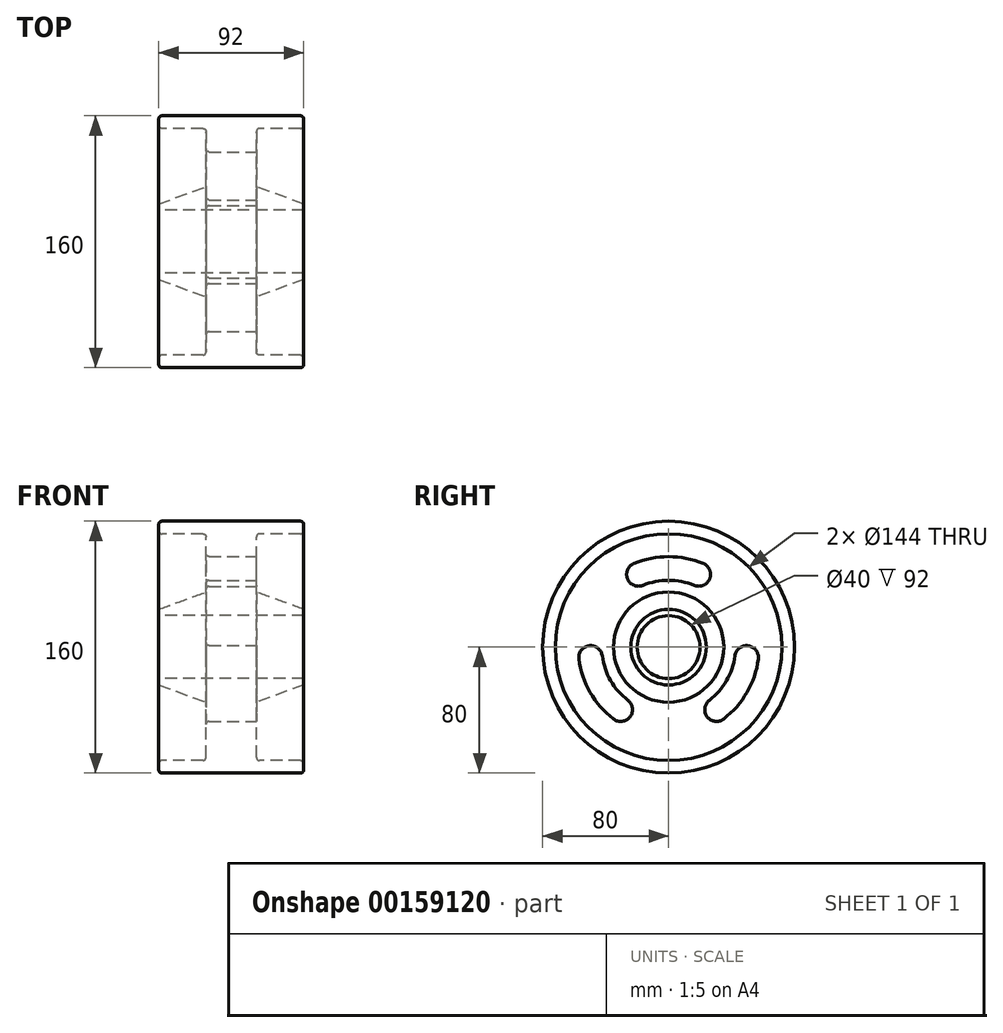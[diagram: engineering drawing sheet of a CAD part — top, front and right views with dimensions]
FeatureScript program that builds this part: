
annotation { "Feature Type Name" : "Feature", "Feature Type Description" : "" }
export const myFeature = defineFeature(function(context is Context, id is Id, definition is map)
    precondition{}
    {
        {
            var Q0;
            Q0=qCreatedBy(makeId("Front.planeOp"),FACE);
            var sketch = newSketch(context, id + "F0", { "sketchPlane" : qUnion([Q0])});
            skLineSegment(sketch, "E0.bottom", {"start": v(0, 0) * mm, "end": v(92, 0) * mm});
            skLineSegment(sketch, "E0.top", {"start": v(0, 80) * mm, "end": v(92, 80) * mm});
            skLineSegment(sketch, "E0.left", {"start": v(0, 0) * mm, "end": v(0, 80) * mm});
            skLineSegment(sketch, "E0.right", {"start": v(92, 0) * mm, "end": v(92, 80) * mm});
            skLineSegment(sketch, "E1", {"start": v(0, 72) * mm, "end": v(30, 72) * mm});
            skLineSegment(sketch, "E2", {"start": v(30, 72) * mm, "end": v(30, 35) * mm});
            skLineSegment(sketch, "E3", {"start": v(30, 35) * mm, "end": v(0, 24) * mm});
            skLineSegment(sketch, "E4", {"start": v(0, 20) * mm, "end": v(92, 20) * mm});
            skLineSegment(sketch, "E5", {"start": v(92, 72) * mm, "end": v(62, 72) * mm});
            skLineSegment(sketch, "E6", {"start": v(62, 72) * mm, "end": v(62, 35) * mm});
            skLineSegment(sketch, "E7", {"start": v(62, 35) * mm, "end": v(92, 24) * mm});
            skSolve(sketch);
        }
        {
            var Q0;
            {var subQ2=sQuery(id+"F0.wireOp",EDGE,"E0.top");Q0=makeQuery(id+"F0.imprint","IMPRINT",FACE,{"disambiguationData":[TD([[makeQuery(id+"F0.imprint","IMPRINT",EDGE,{"derivedFrom":subQ2}),-1.0]])]});}
            var Q1;
            Q1=sQuery(id+"F0.wireOp",EDGE,"E0.bottom");
            revolve(context, id + "F1", {"entities" : qUnion([Q0]), "axis" : qUnion([Q1]), "revolveType" : RevolveType.FULL});
        }
        {
            var Q0;
            Q0=makeQuery(id+"F1.opRevolve","SWEPT_FACE",FACE,{"disambiguationData":[OSD([sQuery(id+"F0.wireOp",EDGE,"E6")])]});
            var sketch = newSketch(context, id + "F2", { "sketchPlane" : qUnion([Q0])});
            skCircle(sketch, "E8", {"center": v(0, 0) * mm, "radius": 50 * mm, "construction": true});
            skCircle(sketch, "E9", {"center": v(-19.13, 46.2) * mm, "radius": 7.5 * mm});
            skCircle(sketch, "E10", {"center": v(19.13, 46.2) * mm, "radius": 7.5 * mm});
            skLineSegment(sketch, "E11", {"start": v(0, 0) * mm, "end": v(-19.13, 46.2) * mm, "construction": true});
            skLineSegment(sketch, "E12", {"start": v(0, 0) * mm, "end": v(19.13, 46.2) * mm, "construction": true});
            skLineSegment(sketch, "E13", {"start": v(0, 0) * mm, "end": v(0, 50) * mm, "construction": true});
            skArc(sketch, "E14", {"start": v(16.26, 39.26) * mm, "mid": v(0, 42.5) * mm, "end": v(-16.26, 39.26) * mm});
            skArc(sketch, "E15", {"start": v(22, 53.12) * mm, "mid": v(0, 57.5) * mm, "end": v(-22, 53.12) * mm});
            skLineSegment(sketch, "E16", {"start": v(0, 0) * mm, "end": v(-43.3, -25) * mm, "construction": true});
            skLineSegment(sketch, "E17", {"start": v(0, 0) * mm, "end": v(43.3, -25) * mm, "construction": true});
            skCircle(sketch, "E18", {"center": v(-49.57, -6.53) * mm, "radius": 7.5 * mm});
            skCircle(sketch, "E19", {"center": v(-30.44, -39.67) * mm, "radius": 7.5 * mm});
            skCircle(sketch, "E20", {"center": v(49.57, -6.53) * mm, "radius": 7.5 * mm});
            skCircle(sketch, "E21", {"center": v(30.44, -39.67) * mm, "radius": 7.5 * mm});
            skLineSegment(sketch, "E22", {"start": v(-49.57, -6.53) * mm, "end": v(0, 0) * mm, "construction": true});
            skLineSegment(sketch, "E23", {"start": v(0, 0) * mm, "end": v(-30.44, -39.67) * mm, "construction": true});
            skLineSegment(sketch, "E24", {"start": v(0, 0) * mm, "end": v(30.44, -39.67) * mm, "construction": true});
            skLineSegment(sketch, "E25", {"start": v(0, 0) * mm, "end": v(49.57, -6.53) * mm, "construction": true});
            skCircle(sketch, "E26", {"center": v(0, 0) * mm, "radius": 57.5 * mm});
            skCircle(sketch, "E27", {"center": v(0, 0) * mm, "radius": 42.5 * mm});
            skSolve(sketch);
        }
        {
            var Q0;
            {var subQ0=sQuery(id+"F2.wireOp",EDGE,"E9");var subQ1=makeQuery(id+"F2.imprint","INTERSECT",VERTEX,{"derivedFrom":[subQ0,sQuery(id+"F2.wireOp",EDGE,"E26")]});Q0=makeQuery(id+"F2.imprint","IMPRINT",FACE,{"disambiguationData":[TD([[makeQuery(id+"F2.imprint","IMPRINT",EDGE,{"disambiguationData":[TD([[subQ1,-1.0]])],"derivedFrom":subQ0}),1.0]])]});}
            var Q1;
            {var subQ0=sQuery(id+"F2.wireOp",EDGE,"E26");var subQ1=sQuery(id+"F2.wireOp",EDGE,"E9");var subQ2=makeQuery(id+"F2.imprint","INTERSECT",VERTEX,{"derivedFrom":[subQ1,subQ0]});Q1=makeQuery(id+"F2.imprint","IMPRINT",FACE,{"disambiguationData":[TD([[makeQuery(id+"F2.imprint","IMPRINT",EDGE,{"disambiguationData":[TD([[subQ2,1.0]])],"derivedFrom":subQ1}),-1.0]])]});}
            var Q2;
            {var subQ0=sQuery(id+"F2.wireOp",EDGE,"E10");var subQ1=makeQuery(id+"F2.imprint","INTERSECT",VERTEX,{"derivedFrom":[subQ0,sQuery(id+"F2.wireOp",EDGE,"E26")]});Q2=makeQuery(id+"F2.imprint","IMPRINT",FACE,{"disambiguationData":[TD([[makeQuery(id+"F2.imprint","IMPRINT",EDGE,{"disambiguationData":[TD([[subQ1,-1.0]])],"derivedFrom":subQ0}),1.0]])]});}
            var Q3;
            {var subQ0=sQuery(id+"F2.wireOp",EDGE,"E20");var subQ1=makeQuery(id+"F2.imprint","INTERSECT",VERTEX,{"derivedFrom":[subQ0,sQuery(id+"F2.wireOp",EDGE,"E26")]});Q3=makeQuery(id+"F2.imprint","IMPRINT",FACE,{"disambiguationData":[TD([[makeQuery(id+"F2.imprint","IMPRINT",EDGE,{"disambiguationData":[TD([[subQ1,1.0]])],"derivedFrom":subQ0}),1.0]])]});}
            var Q4;
            {var subQ0=sQuery(id+"F2.wireOp",EDGE,"E26");var subQ1=sQuery(id+"F2.wireOp",EDGE,"E20");var subQ2=makeQuery(id+"F2.imprint","INTERSECT",VERTEX,{"derivedFrom":[subQ1,subQ0]});Q4=makeQuery(id+"F2.imprint","IMPRINT",FACE,{"disambiguationData":[TD([[makeQuery(id+"F2.imprint","IMPRINT",EDGE,{"disambiguationData":[TD([[subQ2,1.0]])],"derivedFrom":subQ1}),-1.0]])]});}
            var Q5;
            {var subQ0=sQuery(id+"F2.wireOp",EDGE,"E21");var subQ1=makeQuery(id+"F2.imprint","INTERSECT",VERTEX,{"derivedFrom":[subQ0,sQuery(id+"F2.wireOp",EDGE,"E26")]});Q5=makeQuery(id+"F2.imprint","IMPRINT",FACE,{"disambiguationData":[TD([[makeQuery(id+"F2.imprint","IMPRINT",EDGE,{"disambiguationData":[TD([[subQ1,1.0]])],"derivedFrom":subQ0}),1.0]])]});}
            var Q6;
            {var subQ0=sQuery(id+"F2.wireOp",EDGE,"E18");var subQ1=makeQuery(id+"F2.imprint","INTERSECT",VERTEX,{"derivedFrom":[subQ0,sQuery(id+"F2.wireOp",EDGE,"E26")]});Q6=makeQuery(id+"F2.imprint","IMPRINT",FACE,{"disambiguationData":[TD([[makeQuery(id+"F2.imprint","IMPRINT",EDGE,{"disambiguationData":[TD([[subQ1,1.0]])],"derivedFrom":subQ0}),1.0]])]});}
            var Q7;
            {var subQ0=sQuery(id+"F2.wireOp",EDGE,"E26");var subQ1=sQuery(id+"F2.wireOp",EDGE,"E18");var subQ2=makeQuery(id+"F2.imprint","INTERSECT",VERTEX,{"derivedFrom":[subQ1,subQ0]});Q7=makeQuery(id+"F2.imprint","IMPRINT",FACE,{"disambiguationData":[TD([[makeQuery(id+"F2.imprint","IMPRINT",EDGE,{"disambiguationData":[TD([[subQ2,-1.0]])],"derivedFrom":subQ1}),-1.0]])]});}
            var Q8;
            {var subQ0=sQuery(id+"F2.wireOp",EDGE,"E19");var subQ1=makeQuery(id+"F2.imprint","INTERSECT",VERTEX,{"derivedFrom":[subQ0,sQuery(id+"F2.wireOp",EDGE,"E26")]});Q8=makeQuery(id+"F2.imprint","IMPRINT",FACE,{"disambiguationData":[TD([[makeQuery(id+"F2.imprint","IMPRINT",EDGE,{"disambiguationData":[TD([[subQ1,1.0]])],"derivedFrom":subQ0}),1.0]])]});}
            extrude(context, id + "F3", {"entities" : qUnion([Q0, Q1, Q2, Q3, Q4, Q5, Q6, Q7, Q8]), "operationType" : NewBodyOperationType.REMOVE, "endBound" : BoundingType.THROUGH_ALL, "oppositeDirection" : true, "depth" : 25 * mm});
        }
        {
            var Q0;
            Q0=makeQuery(id+"F1.opRevolve","SWEPT_EDGE",EDGE,{"disambiguationData":[OSD([sQuery(id+"F0.wireOp",EDGE,"E0.top"),sQuery(id+"F0.wireOp",EDGE,"E0.right")])]});
            var Q1;
            Q1=makeQuery(id+"F1.opRevolve","SWEPT_EDGE",EDGE,{"disambiguationData":[OSD([sQuery(id+"F0.wireOp",EDGE,"E0.right"),sQuery(id+"F0.wireOp",EDGE,"E5")])]});
            var Q2;
            Q2=makeQuery(id+"F1.opRevolve","SWEPT_EDGE",EDGE,{"disambiguationData":[OSD([sQuery(id+"F0.wireOp",EDGE,"E0.top"),sQuery(id+"F0.wireOp",EDGE,"E0.left")])]});
            var Q3;
            Q3=makeQuery(id+"F1.opRevolve","SWEPT_EDGE",EDGE,{"disambiguationData":[OSD([sQuery(id+"F0.wireOp",EDGE,"E0.left"),sQuery(id+"F0.wireOp",EDGE,"E1")])]});
            var Q4;
            Q4=makeQuery(id+"F1.opRevolve","SWEPT_EDGE",EDGE,{"disambiguationData":[OSD([sQuery(id+"F0.wireOp",EDGE,"E1"),sQuery(id+"F0.wireOp",EDGE,"E2")])]});
            var Q5;
            Q5=makeQuery(id+"F1.opRevolve","SWEPT_EDGE",EDGE,{"disambiguationData":[OSD([sQuery(id+"F0.wireOp",EDGE,"E5"),sQuery(id+"F0.wireOp",EDGE,"E6")])]});
            var Q6;
            {var subQ0=sQuery(id+"F2.wireOp",EDGE,"E26");Q6=makeQuery(id+"F3.boolean.opBoolean","COPY",EDGE,{"derivedFrom":makeQuery(id+"F3.opExtrude","CAP_EDGE",EDGE,{"disambiguationData":[OSD([subQ0]),TDD([makeQuery(id+"F2.imprint","IMPRINT",EDGE,{"disambiguationData":[TD([[makeQuery(id+"F2.imprint","INTERSECT",VERTEX,{"derivedFrom":[sQuery(id+"F2.wireOp",EDGE,"E9"),subQ0]}),1.0]])],"derivedFrom":subQ0})])],"isStart":true})});}
            var Q7;
            Q7=makeQuery(id+"F3.boolean.opBoolean","COPY",EDGE,{"derivedFrom":makeQuery(id+"F3.opExtrude","CAP_EDGE",EDGE,{"disambiguationData":[OSD([sQuery(id+"F2.wireOp",EDGE,"E20")])],"isStart":true})});
            var Q8;
            Q8=makeQuery(id+"F3.boolean.opBoolean","COPY",EDGE,{"derivedFrom":makeQuery(id+"F3.opExtrude","CAP_EDGE",EDGE,{"disambiguationData":[OSD([sQuery(id+"F2.wireOp",EDGE,"E18")])],"isStart":true})});
            var Q9;
            Q9=makeQuery(id+"F3.boolean.opBoolean","INTERSECT",EDGE,{"derivedFrom":[makeQuery(id+"F1.opRevolve","SWEPT_FACE",FACE,{"disambiguationData":[OSD([sQuery(id+"F0.wireOp",EDGE,"E2")])]}),makeQuery(id+"F3.opExtrude","SWEPT_FACE",FACE,{"disambiguationData":[OSD([sQuery(id+"F2.wireOp",EDGE,"E10")])]})]});
            var Q10;
            Q10=makeQuery(id+"F3.boolean.opBoolean","INTERSECT",EDGE,{"derivedFrom":[makeQuery(id+"F1.opRevolve","SWEPT_FACE",FACE,{"disambiguationData":[OSD([sQuery(id+"F0.wireOp",EDGE,"E2")])]}),makeQuery(id+"F3.opExtrude","SWEPT_FACE",FACE,{"disambiguationData":[OSD([sQuery(id+"F2.wireOp",EDGE,"E20")])]})]});
            var Q11;
            Q11=makeQuery(id+"F3.boolean.opBoolean","INTERSECT",EDGE,{"derivedFrom":[makeQuery(id+"F1.opRevolve","SWEPT_FACE",FACE,{"disambiguationData":[OSD([sQuery(id+"F0.wireOp",EDGE,"E2")])]}),makeQuery(id+"F3.opExtrude","SWEPT_FACE",FACE,{"disambiguationData":[OSD([sQuery(id+"F2.wireOp",EDGE,"E18")])]})]});
            fillet(context, id + "F4", {"entities" : qUnion([Q0, Q1, Q2, Q3, Q4, Q5, Q6, Q7, Q8, Q9, Q10, Q11]), "radius" : 2 * mm, "tangentPropagation" : true, "allowEdgeOverflow" : false});
        }
    });
